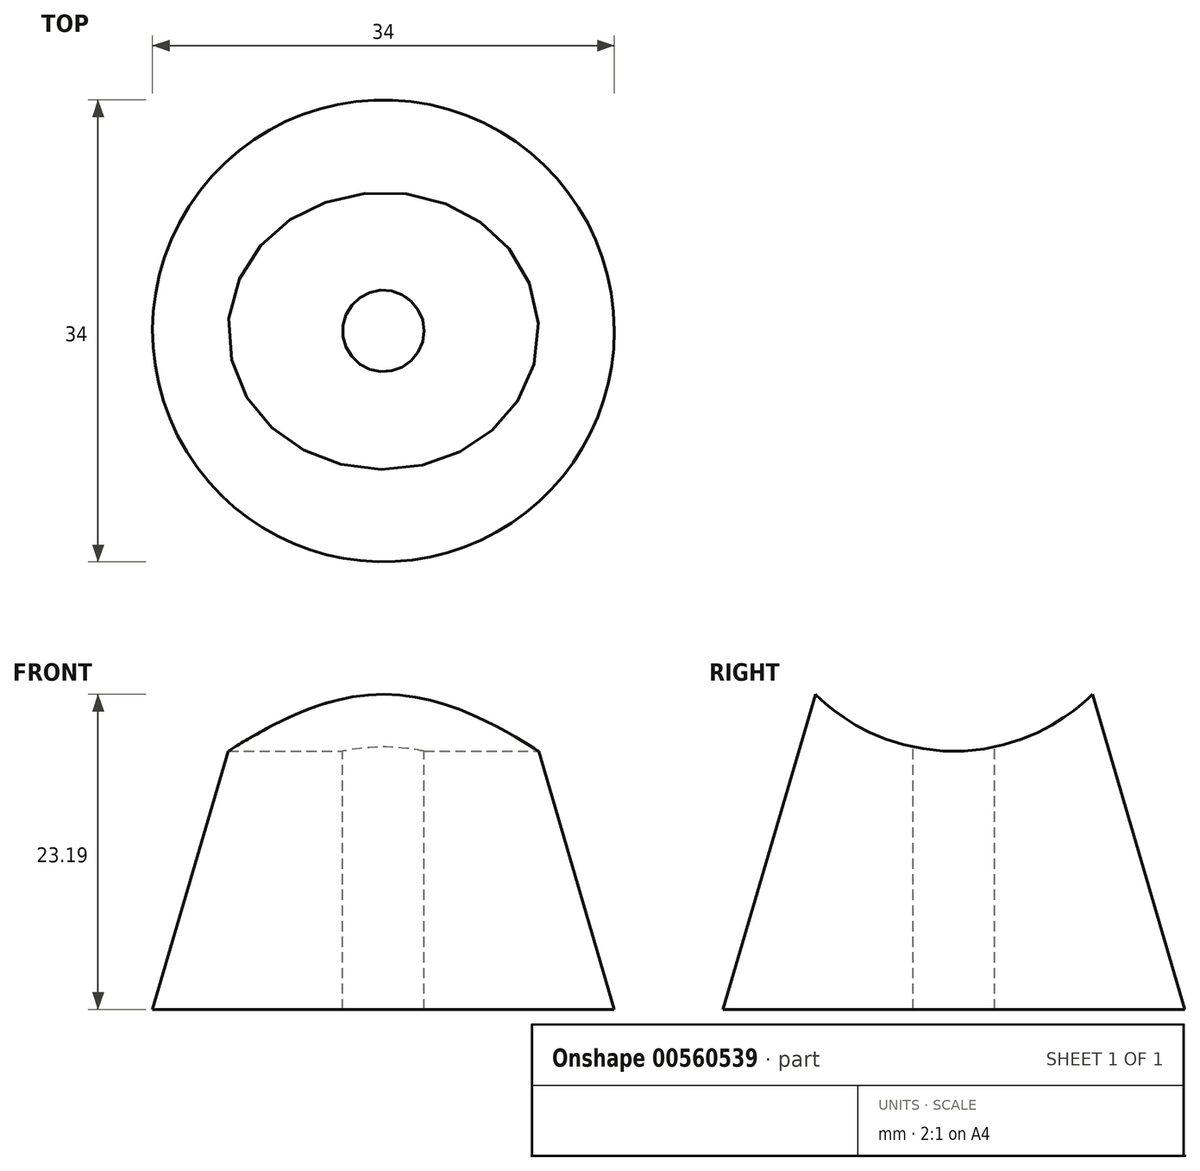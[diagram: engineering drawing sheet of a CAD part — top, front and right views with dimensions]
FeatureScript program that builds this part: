
annotation { "Feature Type Name" : "Feature", "Feature Type Description" : "" }
export const myFeature = defineFeature(function(context is Context, id is Id, definition is map)
    precondition{}
    {
        {
            var Q0;
            Q0=qCreatedBy(makeId("Right.planeOp"),FACE);
            var sketch = newSketch(context, id + "F0", { "sketchPlane" : qUnion([Q0])});
            skLineSegment(sketch, "E0", {"start": v(-3, 0) * mm, "end": v(-3, 19.31) * mm});
            skLineSegment(sketch, "E1", {"start": v(-3, 0) * mm, "end": v(-17, 0) * mm});
            skLineSegment(sketch, "E2", {"start": v(0, 19) * mm, "end": v(0, 0) * mm});
            skCircle(sketch, "E3", {"center": v(0, 33.5) * mm, "radius": 14.5 * mm});
            skPoint(sketch, "E4", {"position": v(0, 0) * mm});
            skLineSegment(sketch, "E5", {"start": v(-10.2, 23.19) * mm, "end": v(-17, 0) * mm});
            skSolve(sketch);
        }
        {
            var Q0;
            {var subQ0=sQuery(id+"F0.wireOp",EDGE,"E0");Q0=makeQuery(id+"F0.imprint","IMPRINT",FACE,{"disambiguationData":[TD([[makeQuery(id+"F0.imprint","IMPRINT",EDGE,{"derivedFrom":subQ0}),1.0]])]});}
            var Q1;
            Q1=sQuery(id+"F0.wireOp",EDGE,"E2");
            revolve(context, id + "F1", {"entities" : qUnion([Q0]), "axis" : qUnion([Q1]), "revolveType" : RevolveType.FULL});
        }
        {
            var Q0;
            {var subQ0=sQuery(id+"F0.wireOp",EDGE,"E3");var subQ3=makeQuery(id+"F0.imprint","IMPRINT",VERTEX,{"derivedFrom":subQ0});Q0=makeQuery(id+"F0.imprint","IMPRINT",FACE,{"disambiguationData":[TD([[makeQuery(id+"F0.imprint","IMPRINT",EDGE,{"disambiguationData":[TD([[subQ3,1.0]])],"derivedFrom":subQ0}),1.0]])]});}
            extrude(context, id + "F2", {"entities" : qUnion([Q0]), "operationType" : NewBodyOperationType.REMOVE, "endBound" : BoundingType.SYMMETRIC, "oppositeDirection" : true, "depth" : 30 * mm, "offsetDistance" : 25 * mm});
        }
    });
